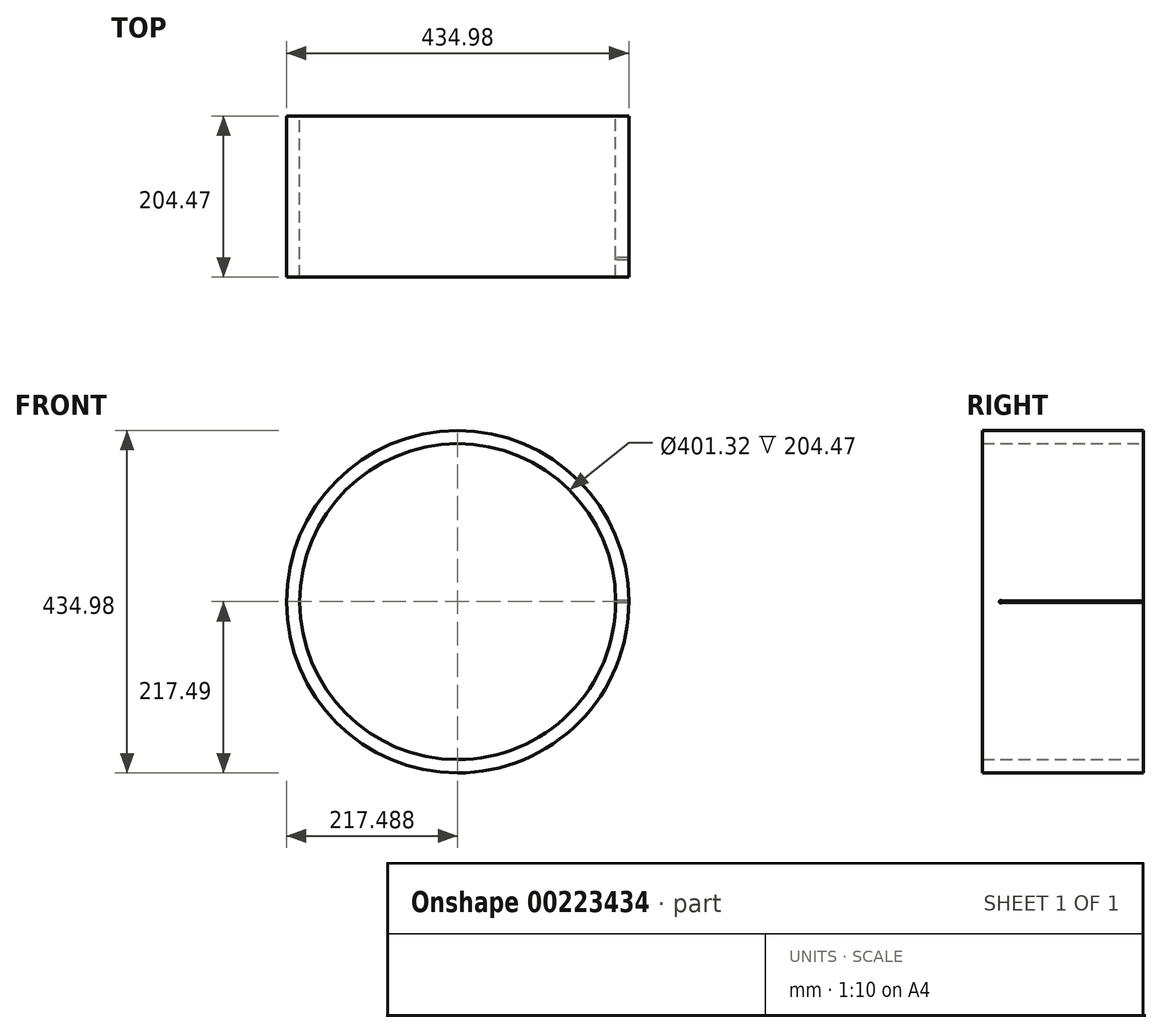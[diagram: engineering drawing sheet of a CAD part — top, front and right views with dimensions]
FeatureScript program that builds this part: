
annotation { "Feature Type Name" : "Feature", "Feature Type Description" : "" }
export const myFeature = defineFeature(function(context is Context, id is Id, definition is map)
    precondition{}
    {
        {
            var Q0;
            Q0=qCreatedBy(makeId("Front.planeOp"),FACE);
            var sketch = newSketch(context, id + "F0", { "sketchPlane" : qUnion([Q0])});
            skCircle(sketch, "E0", {"center": v(0, 0) * mm, "radius": 7.9 * mm});
            skCircle(sketch, "E1", {"center": v(0, 0) * mm, "radius": 8.56 * mm});
            skSolve(sketch);
        }
        {
            var Q0;
            Q0=makeQuery(id+"F0.imprint","IMPRINT",FACE,{"disambiguationData":[TD([[makeQuery(id+"F0.imprint","IMPRINT",EDGE,{"derivedFrom":sQuery(id+"F0.wireOp",EDGE,"E0")}),-1.0]])]});
            extrude(context, id + "F1", {"entities" : qUnion([Q0]), "depth" : 8.05 * mm});
        }
        {
            var Q0;
            Q0=qCreatedBy(makeId("Right.planeOp"),FACE);
            var sketch = newSketch(context, id + "F2", { "sketchPlane" : qUnion([Q0])});
            skLineSegment(sketch, "E2.0", {"start": v(0, 0.03) * mm, "end": v(-7.09, 0.03) * mm});
            skLineSegment(sketch, "E3.0", {"start": v(0, -0.03) * mm, "end": v(-7.09, -0.03) * mm});
            skArc(sketch, "E4", {"start": v(-7.09, 0.03) * mm, "mid": v(-7.2, 0) * mm, "end": v(-7.09, -0.03) * mm});
            skLineSegment(sketch, "E5", {"start": v(0, 0.03) * mm, "end": v(0.06, 0.03) * mm});
            skLineSegment(sketch, "E6", {"start": v(0.06, 0.03) * mm, "end": v(0.06, -0.04) * mm});
            skLineSegment(sketch, "E7", {"start": v(0.06, -0.04) * mm, "end": v(0, -0.03) * mm});
            skSolve(sketch);
        }
        {
            var Q0;
            Q0 = qSketchRegion(id + "F2", true);
            extrude(context, id + "F3", {"entities" : qUnion([Q0]), "operationType" : NewBodyOperationType.REMOVE, "depth" : 25 * mm});
        }
        {
            var Q0;
            Q0=makeQuery(id+"F1.opExtrude","CAP_FACE",FACE,{"disambiguationData":[OSD([sQuery(id+"F0.wireOp",EDGE,"E0"),sQuery(id+"F0.wireOp",EDGE,"E1")])],"isStart":true});
            var sketch = newSketch(context, id + "F4", { "sketchPlane" : qUnion([Q0])});
            skCircle(sketch, "E8", {"center": v(0.22, 0) * mm, "radius": 9.59 * mm});
            skSolve(sketch);
        }
        {
            var Q0;
            Q0=makeQuery(id+"F1.opExtrude","SWEPT_BODY",BODY,{"disambiguationData":[OSD([sQuery(id+"F0.wireOp",EDGE,"E0"),sQuery(id+"F0.wireOp",EDGE,"E1")])]});
            var Q1;
            Q1=sQuery(id+"F4.wireOp",VERTEX,"E8.center");
            transform(context, id + "F5", {"entities" : qUnion([Q0]), "transformType" : TransformType.SCALE_UNIFORMLY, "scale" : 25.4, "scalePoint" : qUnion([Q1]), "makeCopy" : false});
        }
    });
